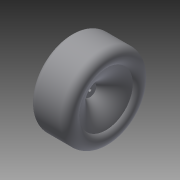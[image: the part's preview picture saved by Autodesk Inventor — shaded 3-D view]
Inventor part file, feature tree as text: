
AUTODESK INVENTOR PART (.ipt)
format: ipt  version: 2015 (Build 190159000, 159)  size: 194,560 bytes
history: native  units: mm
features: fillet x3, sketch x2, revolve x1, extrude x1
ambient origin geometry x8: Origin, YZ Plane, XZ Plane, XY Plane, X Axis, Y Axis, Z Axis, Center Point
bodies: Solid1 (feature_tree)
feature tree (7):
  revolve  "Revolution1"  [1 undecoded]
  extrude  "Extrusion1"  Depth=11.25mm
  fillet  "Fillet1"  Radius=10.0mm
  fillet  "Fillet2"  Radius=10.0mm
  fillet  "Fillet3"  Radius=9.25mm
  sketch  "Sketch1"  dims[d9=4.0mm d12=5.0mm]
  sketch  "Sketch2"  dims[d15=90.0deg d16=4.2mm d17=10.0mm d18=0.0mm d19=10.0mm d20=9.25mm d21=11.25mm]
note: 1 required parameter value undecoded (feature->parameter linkage not recoverable at this tier; creation-order binding heuristic only, values carry confidence <= 0.55)
